# Revit family: Haworth_CabanaLounge_Table_Rectangle
name_source: partatom
category: Furniture
revit_build: Autodesk Revit 2018 (Build: 20170223_1515(x64)
units: mm (PartAtom-declared; Revit-internal decimal feet)

## family parameters
Always vertical = Yes
Cut with Voids When Loaded = No
OmniClass Number = 23.40.70.14.64.21
OmniClass Title = Systems Furniture
Room Calculation Point = No
Shared = No
Work Plane-Based = No

## types (8) — shared parameters
Assembly Code = E2020200
Manufacturer = Haworth
Model = Haworth Cabana
Revision Number = 1
Size = Verify Final Dim. w/ Haworth
Table Depth = 30"
URL = http://www.haworth.com
URL - Product = https://www.haworth.com
Warranty = http://www.haworth.com

## per-type parameters (varying)
| type | Actual Depth | Actual Height | Actual Width | Description | High Screen | Low Screen | No Screen | Rectangle | Screen Width | Square | Table Height | Table Width | With Screen | With Top |
| S922 - Square Tiered - High Screen | 32" | 54" | 32" | Haworth Cabana Table - Square Tiered - High Screen | Yes | No | No | No | 32" | Yes | 15 11/16" | 30" | Yes | Yes |
| S920 - Square Tiered - No Screen | 30" | 15 11/16" | 30" | Haworth Cabana Table - Square Tiered - No Screen | No | No | Yes | No | 32" | Yes | 15 11/16" | 30" | No | Yes |
| S942 - Rectangle Tiered - High Screen | 32" | 54" | 23" | Haworth Cabana Table - Rectangle Tiered - High Screen | Yes | No | No | Yes | 23" | No | 15 11/16" | 21" | Yes | Yes |
| S940 - Rectangle Tiered - No Screen | 30" | 15 11/16" | 21" | Haworth Cabana Table - Rectangle Tiered - No Screen | No | No | Yes | Yes | 23" | No | 15 11/16" | 21" | No | Yes |
| S930 - Rectangle - No Screen | 30" | 11 5/16" | 21" | Haworth Cabana Table - Rectangle - No Screen | No | No | Yes | Yes | 23" | No | 11 5/16" | 21" | No | No |
| S931 - Rectangle - Low Screen | 32" | 42" | 23" | Haworth Cabana Table - Rectangle - Low Screen | No | Yes | No | Yes | 23" | No | 11 5/16" | 21" | Yes | No |
| S911 - Square - Low Screen | 32" | 42" | 32" | Haworth Cabana Table - Square - Low Screen | No | Yes | No | No | 32" | Yes | 11 5/16" | 30" | Yes | No |
| S910 - Square - No Screen | 30" | 11 5/16" | 30" | Haworth Cabana Table - Square - No Screen | No | No | Yes | No | 32" | Yes | 11 5/16" | 30" | No | No |

## geometry (parser evidence)
native form markers: Extrusion x1, Sweep x11
no freeform markers — native parametric forms only
